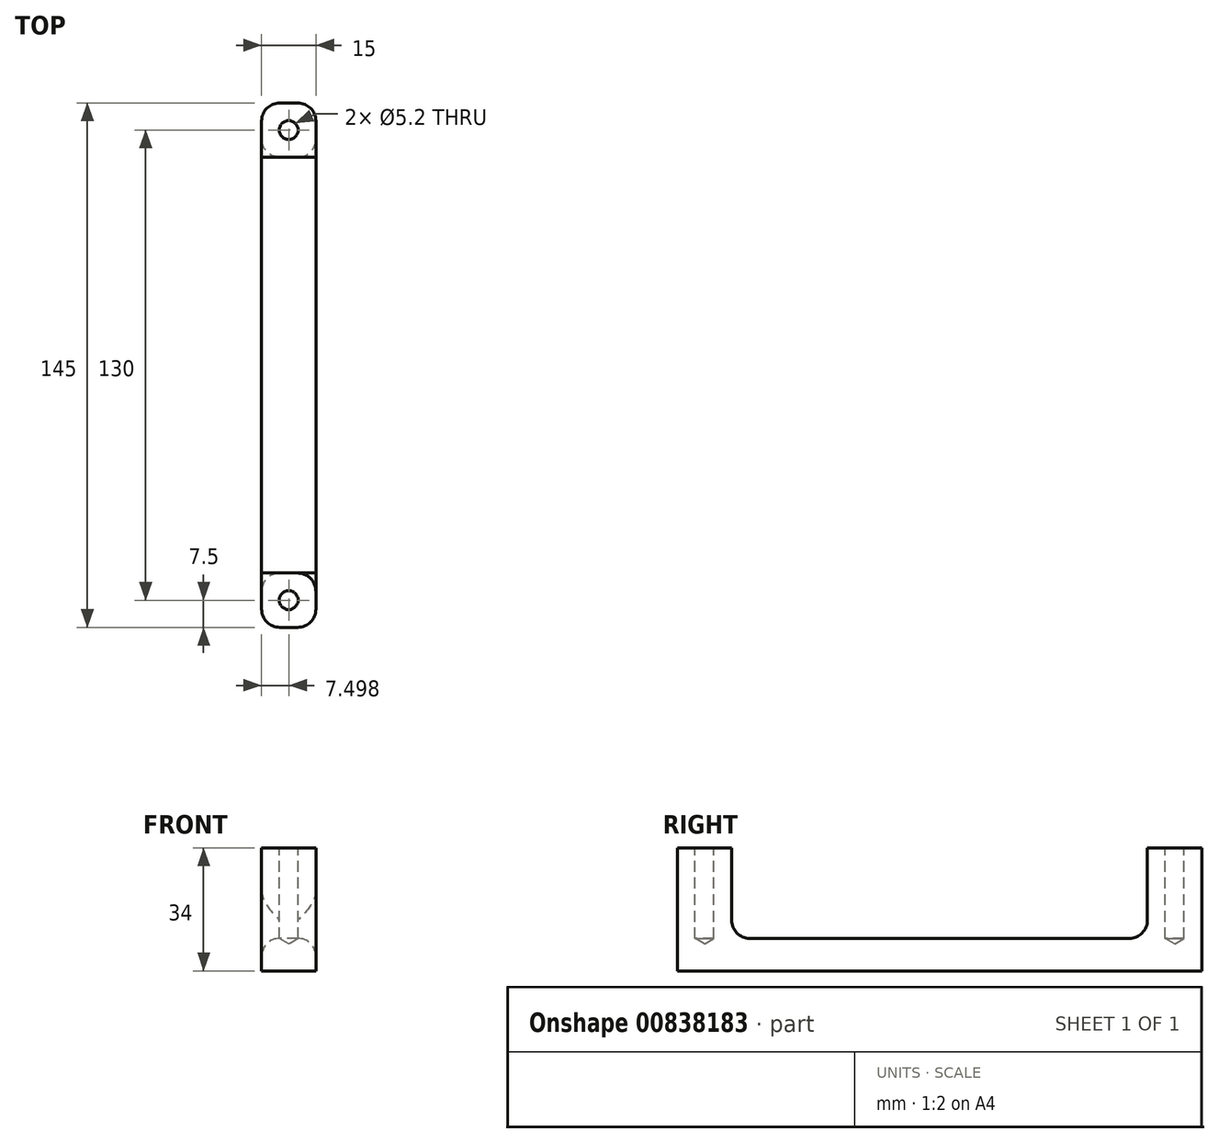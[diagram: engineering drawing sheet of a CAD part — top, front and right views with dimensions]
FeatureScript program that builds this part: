
annotation { "Feature Type Name" : "Feature", "Feature Type Description" : "" }
export const myFeature = defineFeature(function(context is Context, id is Id, definition is map)
    precondition{}
    {
        {
            var Q0;
            Q0=qCreatedBy(makeId("Top.planeOp"),FACE);
            var sketch = newSketch(context, id + "F0", { "sketchPlane" : qUnion([Q0])});
            skLineSegment(sketch, "E0.bottom", {"start": v(-56.3, 87.58) * mm, "end": v(-41.3, 87.58) * mm});
            skLineSegment(sketch, "E0.top", {"start": v(-56.3, -57.42) * mm, "end": v(-41.3, -57.42) * mm});
            skLineSegment(sketch, "E0.left", {"start": v(-56.3, 87.58) * mm, "end": v(-56.3, -57.42) * mm});
            skLineSegment(sketch, "E0.right", {"start": v(-41.3, 87.58) * mm, "end": v(-41.3, -57.42) * mm});
            skSolve(sketch);
        }
        {
            var Q0;
            Q0 = qSketchRegion(id + "F0", true);
            extrude(context, id + "F1", {"entities" : qUnion([Q0]), "depth" : 9 * mm, "offsetDistance" : 25 * mm});
        }
        {
            var Q0;
            Q0=makeQuery(id+"F1.opExtrude","CAP_FACE",FACE,{"disambiguationData":[OSD([sQuery(id+"F0.wireOp",EDGE,"E0.bottom"),sQuery(id+"F0.wireOp",EDGE,"E0.top"),sQuery(id+"F0.wireOp",EDGE,"E0.left"),sQuery(id+"F0.wireOp",EDGE,"E0.right")])],"isStart":false});
            var sketch = newSketch(context, id + "F2", { "sketchPlane" : qUnion([Q0])});
            skLineSegment(sketch, "E1", {"start": v(-48.8, 87.58) * mm, "end": v(-48.8, -57.42) * mm, "construction": true});
            skLineSegment(sketch, "E2", {"start": v(-48.8, 15.08) * mm, "end": v(-56.3, 15.08) * mm, "construction": true});
            skLineSegment(sketch, "E3", {"start": v(-56.3, 15.08) * mm, "end": v(-41.3, 15.08) * mm, "construction": true});
            skLineSegment(sketch, "E4.bottom", {"start": v(-56.3, 87.58) * mm, "end": v(-41.3, 87.58) * mm});
            skLineSegment(sketch, "E4.top", {"start": v(-56.3, 72.58) * mm, "end": v(-41.3, 72.58) * mm});
            skLineSegment(sketch, "E4.left", {"start": v(-56.3, 87.58) * mm, "end": v(-56.3, 72.58) * mm});
            skLineSegment(sketch, "E4.right", {"start": v(-41.3, 87.58) * mm, "end": v(-41.3, 72.58) * mm});
            skLineSegment(sketch, "E5", {"start": v(-56.3, -57.42) * mm, "end": v(-41.3, -57.42) * mm});
            skLineSegment(sketch, "E6", {"start": v(-41.3, -57.42) * mm, "end": v(-41.3, -42.42) * mm});
            skLineSegment(sketch, "E7", {"start": v(-41.3, -42.42) * mm, "end": v(-56.3, -42.42) * mm});
            skLineSegment(sketch, "E8", {"start": v(-56.3, -42.42) * mm, "end": v(-56.3, -57.42) * mm});
            skSolve(sketch);
        }
        {
            var Q0;
            Q0=makeQuery(id+"F2.imprint","IMPRINT",FACE,{"disambiguationData":[TD([[makeQuery(id+"F2.imprint","IMPRINT",EDGE,{"derivedFrom":sQuery(id+"F2.wireOp",EDGE,"E5")}),1.0]])]});
            var Q1;
            Q1=makeQuery(id+"F2.imprint","IMPRINT",FACE,{"disambiguationData":[TD([[makeQuery(id+"F2.imprint","IMPRINT",EDGE,{"derivedFrom":sQuery(id+"F2.wireOp",EDGE,"E4.bottom")}),-1.0]])]});
            extrude(context, id + "F3", {"entities" : qUnion([Q0, Q1]), "operationType" : NewBodyOperationType.ADD, "depth" : 25 * mm, "offsetDistance" : 25 * mm});
        }
        {
            var Q0;
            Q0=makeQuery(id+"F3.opExtrude","CAP_FACE",FACE,{"disambiguationData":[OSD([sQuery(id+"F2.wireOp",EDGE,"E5"),sQuery(id+"F2.wireOp",EDGE,"E6"),sQuery(id+"F2.wireOp",EDGE,"E7"),sQuery(id+"F2.wireOp",EDGE,"E8")])],"isStart":false});
            var sketch = newSketch(context, id + "F4", { "sketchPlane" : qUnion([Q0])});
            skLineSegment(sketch, "E9", {"start": v(-56.3, -42.42) * mm, "end": v(-41.3, -57.42) * mm, "construction": true});
            skLineSegment(sketch, "E10", {"start": v(-56.3, -57.42) * mm, "end": v(-41.3, -42.42) * mm});
            skLineSegment(sketch, "E11", {"start": v(-41.3, -42.42) * mm, "end": v(-48.8, -49.92) * mm});
            skSolve(sketch);
        }
        {
            var Q0;
            Q0=makeQuery(id+"F3.opExtrude","CAP_FACE",FACE,{"disambiguationData":[OSD([sQuery(id+"F2.wireOp",EDGE,"E4.bottom"),sQuery(id+"F2.wireOp",EDGE,"E4.top"),sQuery(id+"F2.wireOp",EDGE,"E4.left"),sQuery(id+"F2.wireOp",EDGE,"E4.right")])],"isStart":false});
            var sketch = newSketch(context, id + "F5", { "sketchPlane" : qUnion([Q0])});
            skLineSegment(sketch, "E12", {"start": v(-56.3, 87.58) * mm, "end": v(-41.3, 72.58) * mm, "construction": true});
            skLineSegment(sketch, "E13", {"start": v(-41.3, 72.58) * mm, "end": v(-56.3, 72.58) * mm, "construction": true});
            skLineSegment(sketch, "E14", {"start": v(-56.3, 72.58) * mm, "end": v(-48.8, 80.08) * mm, "construction": true});
            skLineSegment(sketch, "E15", {"start": v(-48.8, 80.08) * mm, "end": v(-41.3, 87.58) * mm, "construction": true});
            skSolve(sketch);
        }
        {
            var Q0;
            Q0=sQuery(id+"F5.wireOp",VERTEX,"E14.end");
            var Q1;
            Q1=sQuery(id+"F4.wireOp",VERTEX,"E11.end");
            var Q2;
            Q2=makeQuery(id+"F1.opExtrude","SWEPT_BODY",BODY,{"disambiguationData":[OSD([sQuery(id+"F0.wireOp",EDGE,"E0.bottom"),sQuery(id+"F0.wireOp",EDGE,"E0.top"),sQuery(id+"F0.wireOp",EDGE,"E0.left"),sQuery(id+"F0.wireOp",EDGE,"E0.right")])]});
            hole(context, id + "F6", {"style" : HoleStyle.SIMPLE, "endStyle" : HoleEndStyle.BLIND, "holeDiameter" : 5.2 * mm, "majorDiameter" : 5 * mm, "holeDepth" : 25 * mm, "isTappedThrough" : true, "tappedDepth" : 12 * mm, "tapClearance" : 3, "locations" : qUnion([Q0, Q1]), "scope" : qUnion([Q2])});
        }
        {
            var Q0;
            Q0=makeQuery(id+"F1.opExtrude","CAP_FACE",FACE,{"disambiguationData":[OSD([sQuery(id+"F0.wireOp",EDGE,"E0.bottom"),sQuery(id+"F0.wireOp",EDGE,"E0.top"),sQuery(id+"F0.wireOp",EDGE,"E0.left"),sQuery(id+"F0.wireOp",EDGE,"E0.right")])],"isStart":false});
            var Q1;
            Q1=makeQuery(id+"F3.boolean.opBoolean","MERGE",EDGE,{"derivedFrom":[makeQuery(id+"F1.opExtrude","SWEPT_EDGE",EDGE,{"disambiguationData":[OSD([sQuery(id+"F0.wireOp",EDGE,"E0.top"),sQuery(id+"F0.wireOp",EDGE,"E0.right")])]}),makeQuery(id+"F3.opExtrude","SWEPT_EDGE",EDGE,{"disambiguationData":[OSD([sQuery(id+"F2.wireOp",EDGE,"E5"),sQuery(id+"F2.wireOp",EDGE,"E6")])]})]});
            var Q2;
            Q2=makeQuery(id+"F3.boolean.opBoolean","MERGE",EDGE,{"derivedFrom":[makeQuery(id+"F1.opExtrude","SWEPT_EDGE",EDGE,{"disambiguationData":[OSD([sQuery(id+"F0.wireOp",EDGE,"E0.top"),sQuery(id+"F0.wireOp",EDGE,"E0.left")])]}),makeQuery(id+"F3.opExtrude","SWEPT_EDGE",EDGE,{"disambiguationData":[OSD([sQuery(id+"F2.wireOp",EDGE,"E5"),sQuery(id+"F2.wireOp",EDGE,"E8")])]})]});
            var Q3;
            Q3=makeQuery(id+"F3.boolean.opBoolean","MERGE",EDGE,{"derivedFrom":[makeQuery(id+"F1.opExtrude","SWEPT_EDGE",EDGE,{"disambiguationData":[OSD([sQuery(id+"F0.wireOp",EDGE,"E0.bottom"),sQuery(id+"F0.wireOp",EDGE,"E0.right")])]}),makeQuery(id+"F3.opExtrude","SWEPT_EDGE",EDGE,{"disambiguationData":[OSD([sQuery(id+"F2.wireOp",EDGE,"E4.bottom"),sQuery(id+"F2.wireOp",EDGE,"E4.right")])]})]});
            var Q4;
            Q4=makeQuery(id+"F3.boolean.opBoolean","MERGE",EDGE,{"derivedFrom":[makeQuery(id+"F1.opExtrude","SWEPT_EDGE",EDGE,{"disambiguationData":[OSD([sQuery(id+"F0.wireOp",EDGE,"E0.bottom"),sQuery(id+"F0.wireOp",EDGE,"E0.left")])]}),makeQuery(id+"F3.opExtrude","SWEPT_EDGE",EDGE,{"disambiguationData":[OSD([sQuery(id+"F2.wireOp",EDGE,"E4.bottom"),sQuery(id+"F2.wireOp",EDGE,"E4.left")])]})]});
            fillet(context, id + "F7", {"entities" : qUnion([Q0, Q1, Q2, Q3, Q4]), "radius" : 5 * mm, "tangentPropagation" : true, "allowEdgeOverflow" : false});
        }
    });
